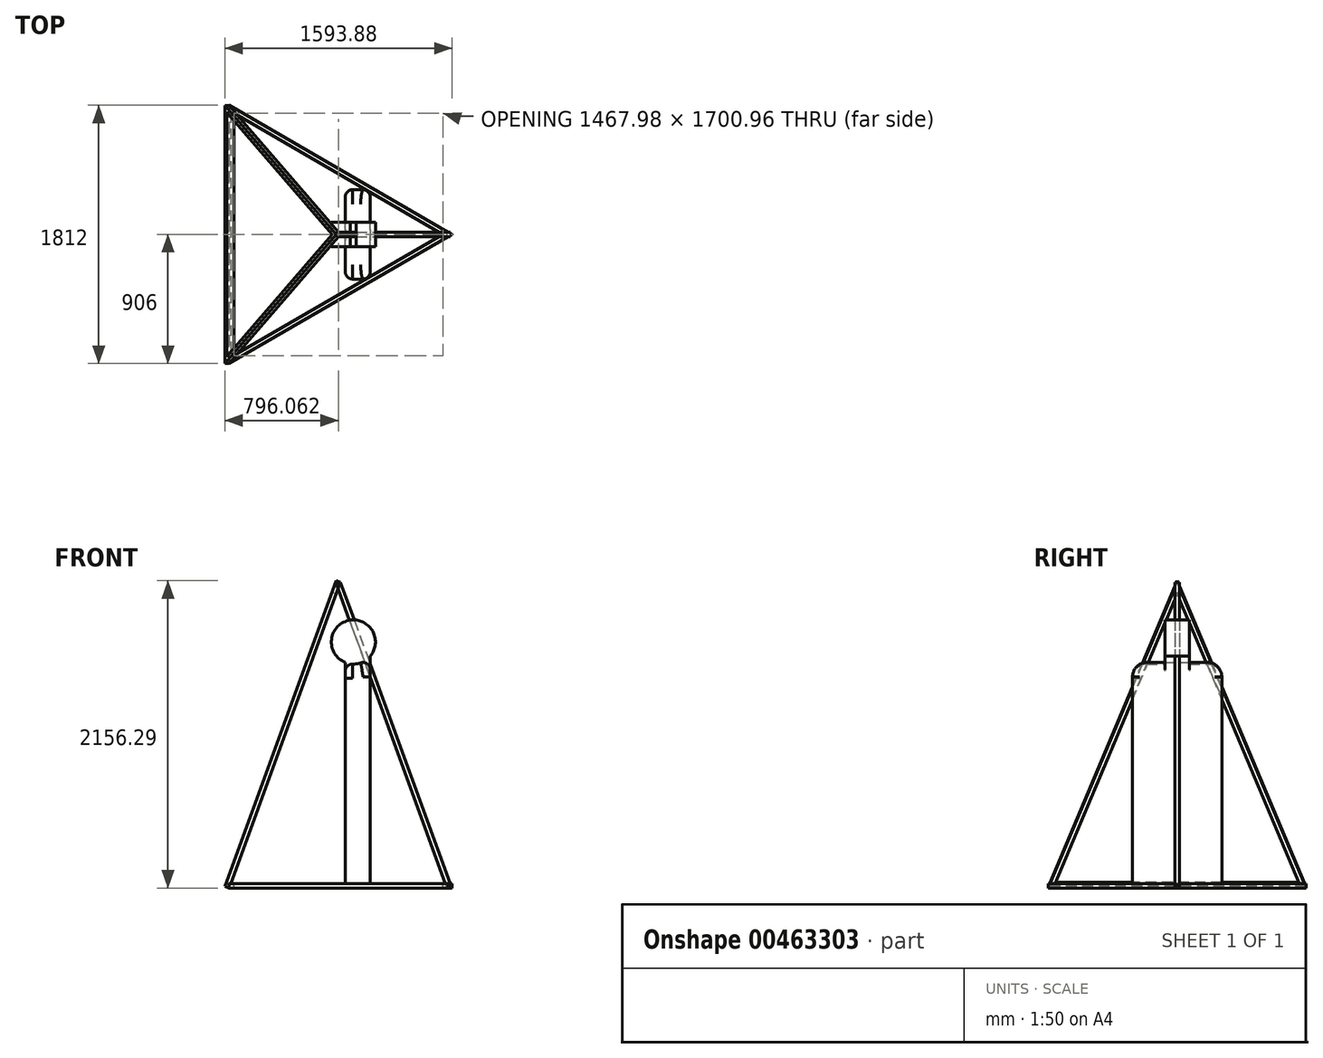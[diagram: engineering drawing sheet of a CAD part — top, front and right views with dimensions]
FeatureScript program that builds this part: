
annotation { "Feature Type Name" : "Feature", "Feature Type Description" : "" }
export const myFeature = defineFeature(function(context is Context, id is Id, definition is map)
    precondition{}
    {
        {
            var Q0;
            Q0=qCreatedBy(makeId("Front.planeOp"),FACE);
            var sketch = newSketch(context, id + "F0", { "sketchPlane" : qUnion([Q0])});
            skArc(sketch, "E0", {"start": v(994.63, 1642.56) * mm, "mid": v(1021.12, 1798.14) * mm, "end": v(897.26, 1895.95) * mm});
            skLineSegment(sketch, "E1.top", {"start": v(994.63, 25.88) * mm, "end": v(820.12, 25.88) * mm});
            skLineSegment(sketch, "E1.left", {"start": v(994.63, 1642.56) * mm, "end": v(994.63, 25.88) * mm});
            skLineSegment(sketch, "E1.right", {"start": v(820.12, 1598.8) * mm, "end": v(820.12, 25.88) * mm});
            skLineSegment(sketch, "E2", {"start": v(897.26, 1895.95) * mm, "end": v(856.29, 1895.95) * mm});
            skArc(sketch, "E3.trimOffspring", {"start": v(856.29, 1895.95) * mm, "mid": v(723.27, 1761.36) * mm, "end": v(820.12, 1598.8) * mm});
            skArc(sketch, "E4", {"start": v(820.12, 1598.8) * mm, "mid": v(914.57, 1591.98) * mm, "end": v(994.63, 1642.56) * mm});
            skSolve(sketch);
        }
        {
            var Q0;
            Q0=makeQuery(id+"F0.imprint","IMPRINT",FACE,{"disambiguationData":[TD([[makeQuery(id+"F0.imprint","IMPRINT",EDGE,{"derivedFrom":sQuery(id+"F0.wireOp",EDGE,"E0")}),1.0]])]});
            extrude(context, id + "F1", {"entities" : qUnion([Q0]), "endBound" : BoundingType.SYMMETRIC, "depth" : 170 * mm});
        }
        {
            var Q0;
            Q0=makeQuery(id+"F0.imprint","IMPRINT",FACE,{"disambiguationData":[TD([[makeQuery(id+"F0.imprint","IMPRINT",EDGE,{"derivedFrom":sQuery(id+"F0.wireOp",EDGE,"E1.top")}),-1.0]])]});
            extrude(context, id + "F2", {"entities" : qUnion([Q0]), "operationType" : NewBodyOperationType.ADD, "endBound" : BoundingType.SYMMETRIC, "depth" : 627 * mm});
        }
        {
            var Q0;
            Q0=qCreatedBy(makeId("Top.planeOp"),FACE);
            var sketch = newSketch(context, id + "F3", { "sketchPlane" : qUnion([Q0])});
            skLineSegment(sketch, "E5", {"start": v(0, -75.76) * mm, "end": v(0, 76.78) * mm});
            skSolve(sketch);
        }
        {
            var Q0;
            Q0=sQuery(id+"F3.wireOp",EDGE,"E5");
            var Q1;
            Q1=qCreatedBy(makeId("Right.planeOp"),FACE);
            cPlane(context, id + "F4", {"entities" : qUnion([Q0, Q1]), "cplaneType" : CPlaneType.LINE_ANGLE, "offset" : 25.4 * mm, "angle" : 20 * degree, "width" : 152.4 * mm, "height" : 152.4 * mm});
        }
        {
            var Q0;
            Q0=qCreatedBy(id+"F4.planeOp",FACE);
            var sketch = newSketch(context, id + "F5", { "sketchPlane" : qUnion([Q0])});
            skLineSegment(sketch, "E6", {"start": v(-904.9, 16.97) * mm, "end": v(0, 16.97) * mm});
            skLineSegment(sketch, "E7", {"start": v(-904.9, 16.97) * mm, "end": v(0, 2300) * mm});
            skLineSegment(sketch, "E8", {"start": v(0, 0) * mm, "end": v(0, 2300) * mm, "construction": true});
            skLineSegment(sketch, "E9", {"start": v(-350, 1416.97) * mm, "end": v(0, 1416.97) * mm, "construction": true});
            skLineSegment(sketch, "E10.MirrorCS", {"start": v(904.9, 16.97) * mm, "end": v(0, 2300) * mm});
            skLineSegment(sketch, "E11.MirrorCS", {"start": v(904.9, 16.97) * mm, "end": v(0, 16.97) * mm});
            skSolve(sketch);
        }
        {
            var Q0;
            Q0=makeQuery(id+"F5.imprint","IMPRINT",FACE,{"disambiguationData":[TD([[makeQuery(id+"F5.imprint","IMPRINT",EDGE,{"derivedFrom":sQuery(id+"F5.wireOp",EDGE,"E6")}),1.0]])]});
            extrude(context, id + "F6", {"entities" : qUnion([Q0]), "depth" : 32 * mm});
        }
        {
            var Q0;
            Q0=makeQuery(id+"F6.opExtrude","CAP_FACE",FACE,{"disambiguationData":[OSD([sQuery(id+"F5.wireOp",EDGE,"E6"),sQuery(id+"F5.wireOp",EDGE,"E7"),sQuery(id+"F5.wireOp",EDGE,"E10.MirrorCS"),sQuery(id+"F5.wireOp",EDGE,"E11.MirrorCS")])],"isStart":false});
            var sketch = newSketch(context, id + "F7", { "sketchPlane" : qUnion([Q0])});
            skLineSegment(sketch, "E12.0", {"start": v(-857.8, 48.97) * mm, "end": v(857.8, 48.97) * mm});
            skLineSegment(sketch, "E12.1", {"start": v(0, 2213.16) * mm, "end": v(-857.8, 48.97) * mm});
            skLineSegment(sketch, "E12.2", {"start": v(857.8, 48.97) * mm, "end": v(0, 2213.16) * mm});
            skSolve(sketch);
        }
        {
            var Q0;
            Q0=makeQuery(id+"F7.imprint","IMPRINT",FACE,{"disambiguationData":[TD([[makeQuery(id+"F7.imprint","IMPRINT",EDGE,{"derivedFrom":sQuery(id+"F7.wireOp",EDGE,"E12.0")}),1.0]])]});
            extrude(context, id + "F8", {"entities" : qUnion([Q0]), "operationType" : NewBodyOperationType.REMOVE, "oppositeDirection" : true, "depth" : 32 * mm});
        }
        {
            var Q0;
            Q0=qCreatedBy(makeId("Front.planeOp"),FACE);
            var sketch = newSketch(context, id + "F9", { "sketchPlane" : qUnion([Q0])});
            skLineSegment(sketch, "E13.bottom", {"start": v(5.8, 47.95) * mm, "end": v(2230.52, 47.95) * mm});
            skLineSegment(sketch, "E13.top", {"start": v(5.8, 15.95) * mm, "end": v(2230.52, 15.95) * mm});
            skLineSegment(sketch, "E13.left", {"start": v(5.8, 47.95) * mm, "end": v(5.8, 15.95) * mm});
            skLineSegment(sketch, "E13.right", {"start": v(2230.52, 47.95) * mm, "end": v(2230.52, 15.95) * mm});
            skSolve(sketch);
        }
        {
            var Q0;
            Q0=makeQuery(id+"F2.opExtrude","CAP_EDGE",EDGE,{"disambiguationData":[OSD([sQuery(id+"F0.wireOp",EDGE,"E4")])],"isStart":true});
            var Q1;
            Q1=makeQuery(id+"F2.opExtrude","CAP_EDGE",EDGE,{"disambiguationData":[OSD([sQuery(id+"F0.wireOp",EDGE,"E4")])],"isStart":false});
            fillet(context, id + "F10", {"entities" : qUnion([Q0, Q1]), "radius" : 100 * mm, "tangentPropagation" : true, "allowEdgeOverflow" : false});
        }
        {
            var Q0;
            Q0=makeQuery(id+"F10.opFillet","BLEND_EDGE",EDGE,{"blendedFrom":[makeQuery(id+"F2.opExtrude","CAP_EDGE",EDGE,{"disambiguationData":[OSD([sQuery(id+"F0.wireOp",EDGE,"E4")])],"isStart":false}),makeQuery(id+"F2.opExtrude","SWEPT_FACE",FACE,{"disambiguationData":[OSD([sQuery(id+"F0.wireOp",EDGE,"E1.right")])]})],"blendedInto":[makeQuery(id+"F2.opExtrude","SWEPT_FACE",FACE,{"disambiguationData":[OSD([sQuery(id+"F0.wireOp",EDGE,"E1.right")])]})]});
            var Q1;
            Q1=makeQuery(id+"F10.opFillet","BLEND_EDGE",EDGE,{"blendedFrom":[makeQuery(id+"F2.opExtrude","CAP_EDGE",EDGE,{"disambiguationData":[OSD([sQuery(id+"F0.wireOp",EDGE,"E4")])],"isStart":false}),makeQuery(id+"F2.opExtrude","SWEPT_FACE",FACE,{"disambiguationData":[OSD([sQuery(id+"F0.wireOp",EDGE,"E1.left")])]})],"blendedInto":[makeQuery(id+"F2.opExtrude","SWEPT_FACE",FACE,{"disambiguationData":[OSD([sQuery(id+"F0.wireOp",EDGE,"E1.left")])]})]});
            var Q2;
            Q2=makeQuery(id+"F10.opFillet","BLEND_EDGE",EDGE,{"blendedFrom":[makeQuery(id+"F2.opExtrude","CAP_EDGE",EDGE,{"disambiguationData":[OSD([sQuery(id+"F0.wireOp",EDGE,"E4")])],"isStart":true}),makeQuery(id+"F2.opExtrude","SWEPT_FACE",FACE,{"disambiguationData":[OSD([sQuery(id+"F0.wireOp",EDGE,"E1.right")])]})],"blendedInto":[makeQuery(id+"F2.opExtrude","SWEPT_FACE",FACE,{"disambiguationData":[OSD([sQuery(id+"F0.wireOp",EDGE,"E1.right")])]})]});
            var Q3;
            Q3=makeQuery(id+"F10.opFillet","BLEND_EDGE",EDGE,{"blendedFrom":[makeQuery(id+"F2.opExtrude","CAP_EDGE",EDGE,{"disambiguationData":[OSD([sQuery(id+"F0.wireOp",EDGE,"E4")])],"isStart":true}),makeQuery(id+"F2.opExtrude","SWEPT_FACE",FACE,{"disambiguationData":[OSD([sQuery(id+"F0.wireOp",EDGE,"E1.left")])]})],"blendedInto":[makeQuery(id+"F2.opExtrude","SWEPT_FACE",FACE,{"disambiguationData":[OSD([sQuery(id+"F0.wireOp",EDGE,"E1.left")])]})]});
            fillet(context, id + "F11", {"entities" : qUnion([Q0, Q1, Q2, Q3]), "radius" : 50 * mm, "tangentPropagation" : true, "allowEdgeOverflow" : false});
        }
        {
            var Q0;
            Q0=qCreatedBy(makeId("Front.planeOp"),FACE);
            var sketch = newSketch(context, id + "F12", { "sketchPlane" : qUnion([Q0])});
            skLineSegment(sketch, "E14", {"start": v(786.65, 2161.3) * mm, "end": v(1562.94, 28.45) * mm});
            skLineSegment(sketch, "E15", {"start": v(786.65, 2161.3) * mm, "end": v(756.58, 2150.35) * mm});
            skLineSegment(sketch, "E16", {"start": v(756.58, 2150.35) * mm, "end": v(1532.87, 17.5) * mm});
            skLineSegment(sketch, "E17", {"start": v(1532.87, 17.5) * mm, "end": v(1562.94, 28.45) * mm});
            skSolve(sketch);
        }
        {
            var Q0;
            Q0=makeQuery(id+"F12.imprint","IMPRINT",FACE,{"disambiguationData":[TD([[makeQuery(id+"F12.imprint","IMPRINT",EDGE,{"derivedFrom":sQuery(id+"F12.wireOp",EDGE,"E14")}),-1.0]])]});
            extrude(context, id + "F13", {"entities" : qUnion([Q0]), "endBound" : BoundingType.SYMMETRIC, "depth" : 32 * mm});
        }
        {
            var Q0;
            Q0=makeQuery(id+"F9.imprint","IMPRINT",FACE,{"disambiguationData":[TD([[makeQuery(id+"F9.imprint","IMPRINT",EDGE,{"derivedFrom":sQuery(id+"F9.wireOp",EDGE,"E13.bottom")}),-1.0]])]});
            extrude(context, id + "F14", {"entities" : qUnion([Q0]), "endBound" : BoundingType.SYMMETRIC, "depth" : 1812 * mm});
        }
        {
            var Q0;
            Q0=makeQuery(id+"F14.opExtrude","SWEPT_FACE",FACE,{"disambiguationData":[OSD([sQuery(id+"F9.wireOp",EDGE,"E13.bottom")])]});
            var sketch = newSketch(context, id + "F15", { "sketchPlane" : qUnion([Q0])});
            skLineSegment(sketch, "E18", {"start": v(5.8, -906) * mm, "end": v(1569.61, 0) * mm});
            skLineSegment(sketch, "E19", {"start": v(1569.61, 0) * mm, "end": v(5.8, 906) * mm});
            skLineSegment(sketch, "E20", {"start": v(5.8, 906) * mm, "end": v(255.5, 1336.98) * mm});
            skLineSegment(sketch, "E21", {"start": v(255.5, 1336.98) * mm, "end": v(3036.03, 1018.39) * mm});
            skLineSegment(sketch, "E22", {"start": v(3036.03, 1018.39) * mm, "end": v(2595.86, -1122.63) * mm});
            skLineSegment(sketch, "E23", {"start": v(2595.86, -1122.63) * mm, "end": v(5.8, -906) * mm});
            skSolve(sketch);
        }
        {
            var Q0;
            Q0=makeQuery(id+"F15.imprint","IMPRINT",FACE,{"disambiguationData":[TD([[makeQuery(id+"F15.imprint","IMPRINT",EDGE,{"derivedFrom":sQuery(id+"F15.wireOp",EDGE,"E20")}),-1.0]])]});
            var Q1;
            Q1=makeQuery(id+"F15.imprint","IMPRINT",FACE,{"disambiguationData":[TD([[makeQuery(id+"F15.imprint","IMPRINT",EDGE,{"derivedFrom":sQuery(id+"F15.wireOp",EDGE,"E18")}),-1.0]])]});
            extrude(context, id + "F16", {"entities" : qUnion([Q0, Q1]), "operationType" : NewBodyOperationType.REMOVE, "oppositeDirection" : true, "depth" : 32 * mm});
        }
        {
            var Q0;
            Q0=makeQuery(id+"F14.opExtrude","SWEPT_FACE",FACE,{"disambiguationData":[OSD([sQuery(id+"F9.wireOp",EDGE,"E13.bottom")])]});
            var sketch = newSketch(context, id + "F17", { "sketchPlane" : qUnion([Q0])});
            skLineSegment(sketch, "E24.0", {"start": v(37.8, -850.48) * mm, "end": v(1505.78, 0) * mm});
            skLineSegment(sketch, "E24.1", {"start": v(37.8, 850.48) * mm, "end": v(37.8, -850.48) * mm});
            skLineSegment(sketch, "E24.2", {"start": v(1505.78, 0) * mm, "end": v(37.8, 850.48) * mm});
            skSolve(sketch);
        }
        {
            var Q0;
            Q0=makeQuery(id+"F17.imprint","IMPRINT",FACE,{"disambiguationData":[TD([[makeQuery(id+"F17.imprint","IMPRINT",EDGE,{"derivedFrom":sQuery(id+"F17.wireOp",EDGE,"E24.0")}),1.0]])]});
            extrude(context, id + "F18", {"entities" : qUnion([Q0]), "operationType" : NewBodyOperationType.REMOVE, "oppositeDirection" : true, "depth" : 32 * mm});
        }
    });
